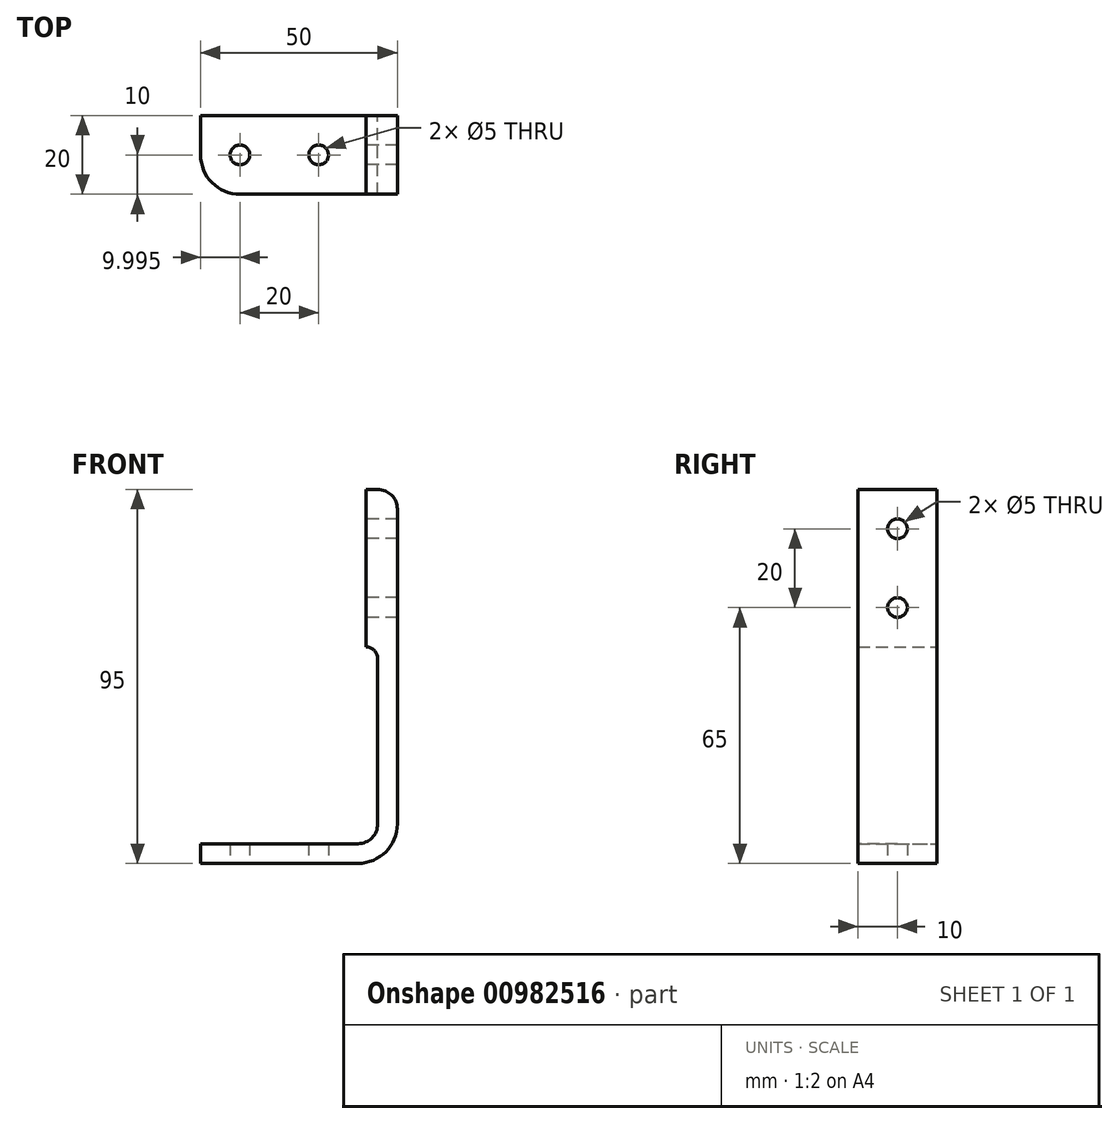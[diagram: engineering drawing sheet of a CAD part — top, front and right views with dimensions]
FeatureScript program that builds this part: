
annotation { "Feature Type Name" : "Feature", "Feature Type Description" : "" }
export const myFeature = defineFeature(function(context is Context, id is Id, definition is map)
    precondition{}
    {
        {
            var Q0;
            Q0=qCreatedBy(makeId("Front.planeOp"),FACE);
            var sketch = newSketch(context, id + "F0", { "sketchPlane" : qUnion([Q0])});
            skLineSegment(sketch, "E0.bottom", {"start": v(-25.06, 5) * mm, "end": v(14.94, 5) * mm});
            skLineSegment(sketch, "E0.top", {"start": v(-25.06, 0) * mm, "end": v(14.94, 0) * mm});
            skLineSegment(sketch, "E0.left", {"start": v(-25.06, 5) * mm, "end": v(-25.06, 0) * mm});
            skLineSegment(sketch, "E0.right", {"start": v(14.94, 5) * mm, "end": v(14.94, 0) * mm});
            skLineSegment(sketch, "E1.bottom", {"start": v(19.94, 10) * mm, "end": v(24.94, 10) * mm});
            skLineSegment(sketch, "E1.top", {"start": v(19.94, 90) * mm, "end": v(24.94, 90) * mm});
            skLineSegment(sketch, "E1.left", {"start": v(19.94, 10) * mm, "end": v(19.94, 90) * mm});
            skLineSegment(sketch, "E1.right", {"start": v(24.94, 10) * mm, "end": v(24.94, 90) * mm});
            skArc(sketch, "E2", {"start": v(14.94, 5) * mm, "mid": v(18.47, 6.46) * mm, "end": v(19.94, 10) * mm});
            skArc(sketch, "E3", {"start": v(14.94, 0) * mm, "mid": v(22, 2.93) * mm, "end": v(24.94, 10) * mm});
            skLineSegment(sketch, "E4.bottom", {"start": v(16.94, 95) * mm, "end": v(19.94, 95) * mm});
            skLineSegment(sketch, "E4.top", {"start": v(16.94, 55) * mm, "end": v(19.94, 55) * mm});
            skLineSegment(sketch, "E4.left", {"start": v(16.94, 95) * mm, "end": v(16.94, 55) * mm});
            skLineSegment(sketch, "E4.right", {"start": v(19.94, 95) * mm, "end": v(19.94, 55) * mm});
            skArc(sketch, "E5", {"start": v(19.94, 95) * mm, "mid": v(23.47, 93.54) * mm, "end": v(24.94, 90) * mm});
            skArc(sketch, "E6", {"start": v(16.94, 55) * mm, "mid": v(19.06, 54.12) * mm, "end": v(19.94, 52) * mm});
            skSolve(sketch);
        }
        {
            var Q0;
            {var subQ4=sQuery(id+"F0.wireOp",EDGE,"E1.bottom");Q0=makeQuery(id+"F0.imprint","IMPRINT",FACE,{"disambiguationData":[TD([[makeQuery(id+"F0.imprint","IMPRINT",EDGE,{"derivedFrom":subQ4}),1.0]])]});}
            var Q1;
            Q1=makeQuery(id+"F0.imprint","IMPRINT",FACE,{"disambiguationData":[TD([[makeQuery(id+"F0.imprint","IMPRINT",EDGE,{"derivedFrom":sQuery(id+"F0.wireOp",EDGE,"E0.bottom")}),-1.0]])]});
            var Q2;
            Q2=makeQuery(id+"F0.imprint","IMPRINT",FACE,{"disambiguationData":[TD([[makeQuery(id+"F0.imprint","IMPRINT",EDGE,{"derivedFrom":sQuery(id+"F0.wireOp",EDGE,"E0.right")}),1.0]])]});
            var Q3;
            {var subQ2=sQuery(id+"F0.wireOp",EDGE,"E4.bottom");Q3=makeQuery(id+"F0.imprint","IMPRINT",FACE,{"disambiguationData":[TD([[makeQuery(id+"F0.imprint","IMPRINT",EDGE,{"derivedFrom":subQ2}),-1.0]])]});}
            var Q4;
            {var subQ0=sQuery(id+"F0.wireOp",EDGE,"E1.top");Q4=makeQuery(id+"F0.imprint","IMPRINT",FACE,{"disambiguationData":[TD([[makeQuery(id+"F0.imprint","IMPRINT",EDGE,{"derivedFrom":subQ0}),1.0]])]});}
            var Q5;
            {var subQ0=sQuery(id+"F0.wireOp",EDGE,"E4.top");Q5=makeQuery(id+"F0.imprint","IMPRINT",FACE,{"disambiguationData":[TD([[makeQuery(id+"F0.imprint","IMPRINT",EDGE,{"derivedFrom":subQ0}),-1.0]])]});}
            var Q6;
            Q6 = qSketchRegion(id + "F2", true);
            extrude(context, id + "F1", {"entities" : qUnion([Q0, Q1, Q2, Q3, Q4, Q5, Q6]), "depth" : 20 * mm, "offsetDistance" : 25 * mm});
        }
        {
            var Q0;
            Q0=qCreatedBy(makeId("Right.planeOp"),FACE);
            var sketch = newSketch(context, id + "F2", { "sketchPlane" : qUnion([Q0])});
            skCircle(sketch, "E7", {"center": v(-10, 85) * mm, "radius": 2.5 * mm});
            skCircle(sketch, "E8", {"center": v(-10, 65) * mm, "radius": 2.5 * mm});
            skSolve(sketch);
        }
        {
            var Q0;
            Q0=sQuery(id+"F2.wireOp",VERTEX,"E7.center");
            var Q1;
            Q1=sQuery(id+"F2.wireOp",VERTEX,"E8.center");
            var Q2;
            Q2=makeQuery(id+"F1.opExtrude","SWEPT_BODY",BODY,{"disambiguationData":[OSD([sQuery(id+"F0.wireOp",EDGE,"E0.bottom"),sQuery(id+"F0.wireOp",EDGE,"E0.top"),sQuery(id+"F0.wireOp",EDGE,"E0.left"),sQuery(id+"F0.wireOp",EDGE,"E1.left"),sQuery(id+"F0.wireOp",EDGE,"E1.right"),sQuery(id+"F0.wireOp",EDGE,"E2"),sQuery(id+"F0.wireOp",EDGE,"E3"),sQuery(id+"F0.wireOp",EDGE,"E4.bottom"),sQuery(id+"F0.wireOp",EDGE,"E4.left"),sQuery(id+"F0.wireOp",EDGE,"E5"),sQuery(id+"F0.wireOp",EDGE,"E6")])]});
            hole(context, id + "F3", {"style" : HoleStyle.SIMPLE, "endStyle" : HoleEndStyle.THROUGH, "oppositeDirection" : true, "holeDiameter" : 5 * mm, "majorDiameter" : 5 * mm, "isTappedThrough" : true, "tappedDepth" : 12 * mm, "tapClearance" : 3, "locations" : qUnion([Q0, Q1]), "scope" : qUnion([Q2])});
        }
        {
            var Q0;
            Q0=qCreatedBy(makeId("Top.planeOp"),FACE);
            var sketch = newSketch(context, id + "F4", { "sketchPlane" : qUnion([Q0])});
            skCircle(sketch, "E9", {"center": v(-15.06, -10) * mm, "radius": 2.5 * mm});
            skCircle(sketch, "E10", {"center": v(4.94, -10) * mm, "radius": 2.5 * mm});
            skSolve(sketch);
        }
        {
            var Q0;
            Q0=sQuery(id+"F4.wireOp",VERTEX,"E9.center");
            var Q1;
            Q1=sQuery(id+"F4.wireOp",VERTEX,"E10.center");
            var Q2;
            Q2=makeQuery(id+"F1.opExtrude","SWEPT_BODY",BODY,{"disambiguationData":[OSD([sQuery(id+"F0.wireOp",EDGE,"E0.bottom"),sQuery(id+"F0.wireOp",EDGE,"E0.top"),sQuery(id+"F0.wireOp",EDGE,"E0.left"),sQuery(id+"F0.wireOp",EDGE,"E1.left"),sQuery(id+"F0.wireOp",EDGE,"E1.right"),sQuery(id+"F0.wireOp",EDGE,"E2"),sQuery(id+"F0.wireOp",EDGE,"E3"),sQuery(id+"F0.wireOp",EDGE,"E4.bottom"),sQuery(id+"F0.wireOp",EDGE,"E4.left"),sQuery(id+"F0.wireOp",EDGE,"E5"),sQuery(id+"F0.wireOp",EDGE,"E6")])]});
            hole(context, id + "F5", {"style" : HoleStyle.SIMPLE, "endStyle" : HoleEndStyle.THROUGH, "oppositeDirection" : true, "holeDiameter" : 5 * mm, "majorDiameter" : 5 * mm, "isTappedThrough" : true, "tappedDepth" : 12 * mm, "tapClearance" : 3, "locations" : qUnion([Q0, Q1]), "scope" : qUnion([Q2])});
        }
        {
            var Q0;
            Q0=makeQuery(id+"F1.opExtrude","CAP_EDGE",EDGE,{"disambiguationData":[OSD([sQuery(id+"F0.wireOp",EDGE,"E0.left")])],"isStart":false});
            fillet(context, id + "F6", {"entities" : qUnion([Q0]), "radius" : 10 * mm, "tangentPropagation" : true, "allowEdgeOverflow" : false});
        }
    });
